# Revit family: Deli
name_source: partatom
category: Мебель
revit_build: Autodesk Revit 2017 (Build: 20160225_1515(x64)
units: mm (PartAtom-declared; Revit-internal decimal feet)

## family parameters
Всегда вертикально = Да
Заголовок OmniClass = General Furniture and Specialties
На основе рабочей плоскости = Нет
Номер OmniClass = 23.40.20.00
Общий = Нет
При загрузке вырезать с полостями = Нет
Точка расчета площади = Нет

## types (9) — shared parameters
Изготовитель = Skandiform AB
Ключевая пометка = XBF.2
Комментарии к типоразмеру = Created by Astacus AB

## per-type parameters (varying)
| type | Cushion Material | Left Handle | Legs Material | Legs Type | Right Handle | S | Seat Material | URL | Группа модели |
| KS-161 | Skandiform Fabric Blue | Нет | Skandiform  Wood Oak Veneer | Legs 161 | Нет | 0 мм | Skandiform Fabric | www.biminfo.se/?productid=333365 | KS-161 |
| KS-162 | Skandiform Fabric Green | Нет | Skandiform Chrome | Legs 162 | Нет | 0 мм | Skandiform Chrome | http://file-system.ru | KS-162 |
| KS-163 | Light Pink | Нет | White Lacquer | Legs 163 | Нет | 0 мм | Plastic, Opaque White | http://www.skandiform.com | KS-163 |
| KS-165 | Light Pink | Нет | White Lacquer | Legs 165 | Нет | 0 мм | Plastic, Opaque White | http://www.skandiform.com | KS-165 |
| KS-164 | Light Pink | Нет | White Lacquer | Legs 164 | Нет | 0 мм | Plastic, Opaque White | http://www.skandiform.com | KS-164 |
| KS-160 | Skandiform Fabric Blue | Нет | Skandiform Chrome | Legs 160 | Нет | 0 мм | Skandiform Fabric | www.biminfo.se/?productid=333365 | KS-160 |
| KS-160_L | Skandiform Fabric Blue | Да | Skandiform Chrome | Legs 160 | Нет | 2 мм | Skandiform Fabric | www.biminfo.se/?productid=333365 | KS-160_L |
| KS-160_R | Skandiform Fabric Blue | Нет | Skandiform Chrome | Legs 160 | Да | 1 мм | Skandiform Fabric | www.biminfo.se/?productid=333365 | KS-160_R |
| KS-160 LR | Skandiform Fabric Blue | Да | Skandiform Chrome | Legs 160 | Да | 3 мм | Skandiform Fabric | www.biminfo.se/?productid=333365 | KS-160LR |

## geometry (parser evidence)
native form markers: Blend x42, Sweep x18
no freeform markers — native parametric forms only
